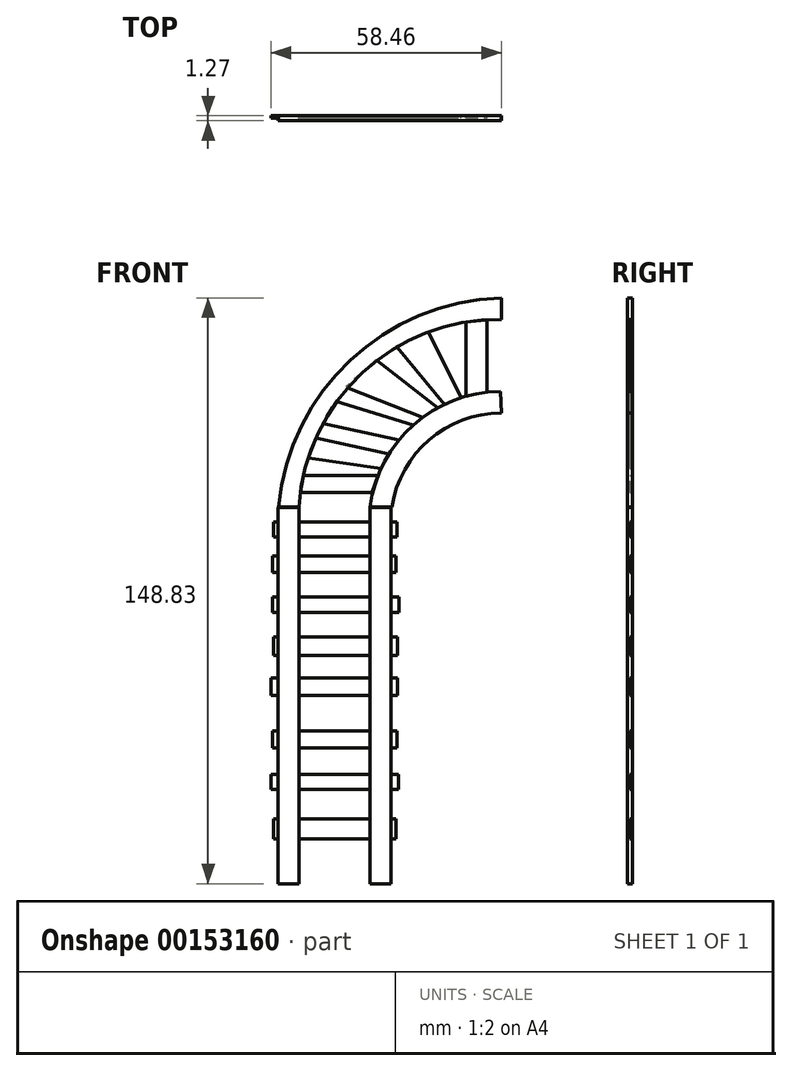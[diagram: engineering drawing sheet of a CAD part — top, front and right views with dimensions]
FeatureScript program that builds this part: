
annotation { "Feature Type Name" : "Feature", "Feature Type Description" : "" }
export const myFeature = defineFeature(function(context is Context, id is Id, definition is map)
    precondition{}
    {
        {
            var Q0;
            Q0=qCreatedBy(makeId("Front.planeOp"),FACE);
            var sketch = newSketch(context, id + "F0", { "sketchPlane" : qUnion([Q0])});
            skLineSegment(sketch, "E0.bottom", {"start": v(4.13, -44.95) * mm, "end": v(9.44, -44.95) * mm});
            skLineSegment(sketch, "E0.top", {"start": v(4.13, 50.63) * mm, "end": v(9.44, 50.63) * mm});
            skLineSegment(sketch, "E0.left", {"start": v(4.13, -44.95) * mm, "end": v(4.13, 50.63) * mm});
            skLineSegment(sketch, "E0.right", {"start": v(9.44, -44.95) * mm, "end": v(9.44, 50.63) * mm});
            skLineSegment(sketch, "E1.bottom", {"start": v(-19.2, -44.95) * mm, "end": v(-13.89, -44.95) * mm});
            skLineSegment(sketch, "E1.top", {"start": v(-19.2, 50.63) * mm, "end": v(-13.89, 50.63) * mm});
            skLineSegment(sketch, "E1.left", {"start": v(-13.89, -44.95) * mm, "end": v(-13.89, 50.63) * mm});
            skLineSegment(sketch, "E1.right", {"start": v(-19.2, -44.95) * mm, "end": v(-19.2, 50.63) * mm});
            skSolve(sketch);
        }
        {
            var Q0;
            Q0 = qSketchRegion(id + "F0", true);
            extrude(context, id + "F1", {"entities" : qUnion([Q0]), "depth" : 1.27 * mm});
        }
        {
            var Q0;
            Q0=qCreatedBy(makeId("Front.planeOp"),FACE);
            var sketch = newSketch(context, id + "F2", { "sketchPlane" : qUnion([Q0])});
            skLineSegment(sketch, "E2.bottom", {"start": v(-20.57, 34.18) * mm, "end": v(10.77, 34.18) * mm});
            skLineSegment(sketch, "E2.top", {"start": v(-20.57, 38.3) * mm, "end": v(10.77, 38.3) * mm});
            skLineSegment(sketch, "E2.left", {"start": v(-20.57, 34.18) * mm, "end": v(-20.57, 38.3) * mm});
            skLineSegment(sketch, "E2.right", {"start": v(10.77, 34.18) * mm, "end": v(10.77, 38.3) * mm});
            skLineSegment(sketch, "E3.bottom", {"start": v(-20.57, 24) * mm, "end": v(11.56, 24) * mm});
            skLineSegment(sketch, "E3.top", {"start": v(-20.57, 27.91) * mm, "end": v(11.56, 27.91) * mm});
            skLineSegment(sketch, "E3.left", {"start": v(-20.57, 24) * mm, "end": v(-20.57, 27.91) * mm});
            skLineSegment(sketch, "E3.right", {"start": v(11.56, 24) * mm, "end": v(11.56, 27.91) * mm});
            skLineSegment(sketch, "E4.bottom", {"start": v(-20.37, 13.02) * mm, "end": v(11.16, 13.02) * mm});
            skLineSegment(sketch, "E4.top", {"start": v(-20.37, 17.73) * mm, "end": v(11.16, 17.73) * mm});
            skLineSegment(sketch, "E4.left", {"start": v(-20.37, 13.02) * mm, "end": v(-20.37, 17.73) * mm});
            skLineSegment(sketch, "E4.right", {"start": v(11.16, 13.02) * mm, "end": v(11.16, 17.73) * mm});
            skLineSegment(sketch, "E5.bottom", {"start": v(-20.96, 2.84) * mm, "end": v(11.16, 2.84) * mm});
            skLineSegment(sketch, "E5.top", {"start": v(-20.96, 7.34) * mm, "end": v(11.16, 7.34) * mm});
            skLineSegment(sketch, "E5.left", {"start": v(-20.96, 2.84) * mm, "end": v(-20.96, 7.34) * mm});
            skLineSegment(sketch, "E5.right", {"start": v(11.16, 2.84) * mm, "end": v(11.16, 7.34) * mm});
            skLineSegment(sketch, "E6.bottom", {"start": v(-20.57, -10.48) * mm, "end": v(10.97, -10.48) * mm});
            skLineSegment(sketch, "E6.top", {"start": v(-20.57, -6.17) * mm, "end": v(10.97, -6.17) * mm});
            skLineSegment(sketch, "E6.left", {"start": v(-20.57, -10.48) * mm, "end": v(-20.57, -6.17) * mm});
            skLineSegment(sketch, "E6.right", {"start": v(10.97, -10.48) * mm, "end": v(10.97, -6.17) * mm});
            skLineSegment(sketch, "E7.bottom", {"start": v(-20.96, -21.06) * mm, "end": v(11.36, -21.06) * mm});
            skLineSegment(sketch, "E7.top", {"start": v(-20.96, -17.14) * mm, "end": v(11.36, -17.14) * mm});
            skLineSegment(sketch, "E7.left", {"start": v(-20.96, -21.06) * mm, "end": v(-20.96, -17.14) * mm});
            skLineSegment(sketch, "E7.right", {"start": v(11.36, -21.06) * mm, "end": v(11.36, -17.14) * mm});
            skLineSegment(sketch, "E8.bottom", {"start": v(-20.37, -33.6) * mm, "end": v(10.77, -33.6) * mm});
            skLineSegment(sketch, "E8.top", {"start": v(-20.37, -28.5) * mm, "end": v(10.77, -28.5) * mm});
            skLineSegment(sketch, "E8.left", {"start": v(-20.37, -33.6) * mm, "end": v(-20.37, -28.5) * mm});
            skLineSegment(sketch, "E8.right", {"start": v(10.77, -33.6) * mm, "end": v(10.77, -28.5) * mm});
            skLineSegment(sketch, "E9.bottom", {"start": v(-20.37, 43.19) * mm, "end": v(10.97, 43.19) * mm});
            skLineSegment(sketch, "E9.top", {"start": v(-20.37, 46.9) * mm, "end": v(10.97, 46.9) * mm});
            skLineSegment(sketch, "E9.left", {"start": v(-20.37, 43.19) * mm, "end": v(-20.37, 46.9) * mm});
            skLineSegment(sketch, "E9.right", {"start": v(10.97, 43.19) * mm, "end": v(10.97, 46.9) * mm});
            skSolve(sketch);
        }
        {
            var Q0;
            Q0 = qSketchRegion(id + "F2", true);
            extrude(context, id + "F3", {"entities" : qUnion([Q0]), "operationType" : NewBodyOperationType.ADD, "depth" : 0.63 * mm});
        }
        {
            var Q0;
            Q0=qCreatedBy(makeId("Front.planeOp"),FACE);
            var sketch = newSketch(context, id + "F4", { "sketchPlane" : qUnion([Q0])});
            skArc(sketch, "E10", {"start": v(37.49, 74.61) * mm, "mid": v(19.18, 67.81) * mm, "end": v(9.7, 50.73) * mm});
            skArc(sketch, "E11", {"start": v(37.27, 80.1) * mm, "mid": v(15.2, 71.63) * mm, "end": v(4.16, 50.72) * mm});
            skLineSegment(sketch, "E12", {"start": v(37.49, 74.61) * mm, "end": v(37.27, 80.1) * mm});
            skLineSegment(sketch, "E13", {"start": v(4.16, 50.72) * mm, "end": v(9.7, 50.73) * mm});
            skSolve(sketch);
        }
        {
            var Q0;
            Q0=qCreatedBy(makeId("Front.planeOp"),FACE);
            var sketch = newSketch(context, id + "F5", { "sketchPlane" : qUnion([Q0])});
            skArc(sketch, "E14", {"start": v(37.5, 98.4) * mm, "mid": v(2.26, 84.9) * mm, "end": v(-13.87, 50.78) * mm});
            skArc(sketch, "E15", {"start": v(37.5, 103.88) * mm, "mid": v(-0.86, 88.05) * mm, "end": v(-19.15, 50.8) * mm});
            skLineSegment(sketch, "E16", {"start": v(-19.15, 50.8) * mm, "end": v(-13.87, 50.78) * mm});
            skLineSegment(sketch, "E17", {"start": v(37.5, 103.88) * mm, "end": v(37.5, 98.4) * mm});
            skSolve(sketch);
        }
        {
            var Q0;
            Q0=qCreatedBy(makeId("Front.planeOp"),FACE);
            var sketch = newSketch(context, id + "F6", { "sketchPlane" : qUnion([Q0])});
            skLineSegment(sketch, "E18", {"start": v(-13.54, 54.4) * mm, "end": v(4.7, 54.4) * mm});
            skLineSegment(sketch, "E19", {"start": v(-12.74, 58.76) * mm, "end": v(6.15, 58.76) * mm});
            skLineSegment(sketch, "E20", {"start": v(-13.54, 54.4) * mm, "end": v(-12.74, 58.76) * mm});
            skLineSegment(sketch, "E21", {"start": v(4.7, 54.4) * mm, "end": v(6.15, 58.76) * mm});
            skLineSegment(sketch, "E22", {"start": v(33.92, 98.34) * mm, "end": v(33.92, 79.88) * mm});
            skLineSegment(sketch, "E23", {"start": v(28.54, 97.74) * mm, "end": v(28.54, 78.92) * mm});
            skLineSegment(sketch, "E24", {"start": v(-1.98, 81.22) * mm, "end": v(17.6, 73.54) * mm});
            skLineSegment(sketch, "E25", {"start": v(5.73, 88.2) * mm, "end": v(21.48, 75.88) * mm});
            skLineSegment(sketch, "E26", {"start": v(10.8, 91.7) * mm, "end": v(23.04, 76.85) * mm});
            skLineSegment(sketch, "E27", {"start": v(18.97, 95.42) * mm, "end": v(27.3, 78.52) * mm});
            skLineSegment(sketch, "E28", {"start": v(28.54, 78.92) * mm, "end": v(33.92, 79.88) * mm});
            skLineSegment(sketch, "E29", {"start": v(28.54, 97.74) * mm, "end": v(33.92, 98.34) * mm});
            skLineSegment(sketch, "E30", {"start": v(23.04, 76.85) * mm, "end": v(27.3, 78.52) * mm});
            skLineSegment(sketch, "E31", {"start": v(10.8, 91.7) * mm, "end": v(18.97, 95.42) * mm});
            skLineSegment(sketch, "E32", {"start": v(17.6, 73.54) * mm, "end": v(21.48, 75.88) * mm});
            skLineSegment(sketch, "E33", {"start": v(5.73, 88.2) * mm, "end": v(-1.98, 81.22) * mm});
            skLineSegment(sketch, "E34", {"start": v(-7.9, 71.99) * mm, "end": v(11.61, 67.78) * mm});
            skLineSegment(sketch, "E35", {"start": v(-4.38, 77.53) * mm, "end": v(15.12, 71.62) * mm});
            skLineSegment(sketch, "E36", {"start": v(11.61, 67.78) * mm, "end": v(15.12, 71.62) * mm});
            skLineSegment(sketch, "E37", {"start": v(-7.9, 71.99) * mm, "end": v(-4.38, 77.53) * mm});
            skLineSegment(sketch, "E38", {"start": v(-9.56, 68.3) * mm, "end": v(9.02, 64.21) * mm});
            skLineSegment(sketch, "E39", {"start": v(-11.57, 63.24) * mm, "end": v(7.07, 60.51) * mm});
            skLineSegment(sketch, "E40", {"start": v(7.07, 60.51) * mm, "end": v(9.02, 64.21) * mm});
            skLineSegment(sketch, "E41", {"start": v(-11.57, 63.24) * mm, "end": v(-9.56, 68.3) * mm});
            skSolve(sketch);
        }
        {
            var Q0;
            Q0 = qSketchRegion(id + "F4", true);
            var Q1;
            Q1 = qSketchRegion(id + "F5", true);
            extrude(context, id + "F7", {"entities" : qUnion([Q0, Q1]), "operationType" : NewBodyOperationType.ADD, "depth" : 1.27 * mm});
        }
        {
            var Q0;
            Q0 = qSketchRegion(id + "F6", true);
            extrude(context, id + "F8", {"entities" : qUnion([Q0]), "depth" : 0.63 * mm});
        }
    });
